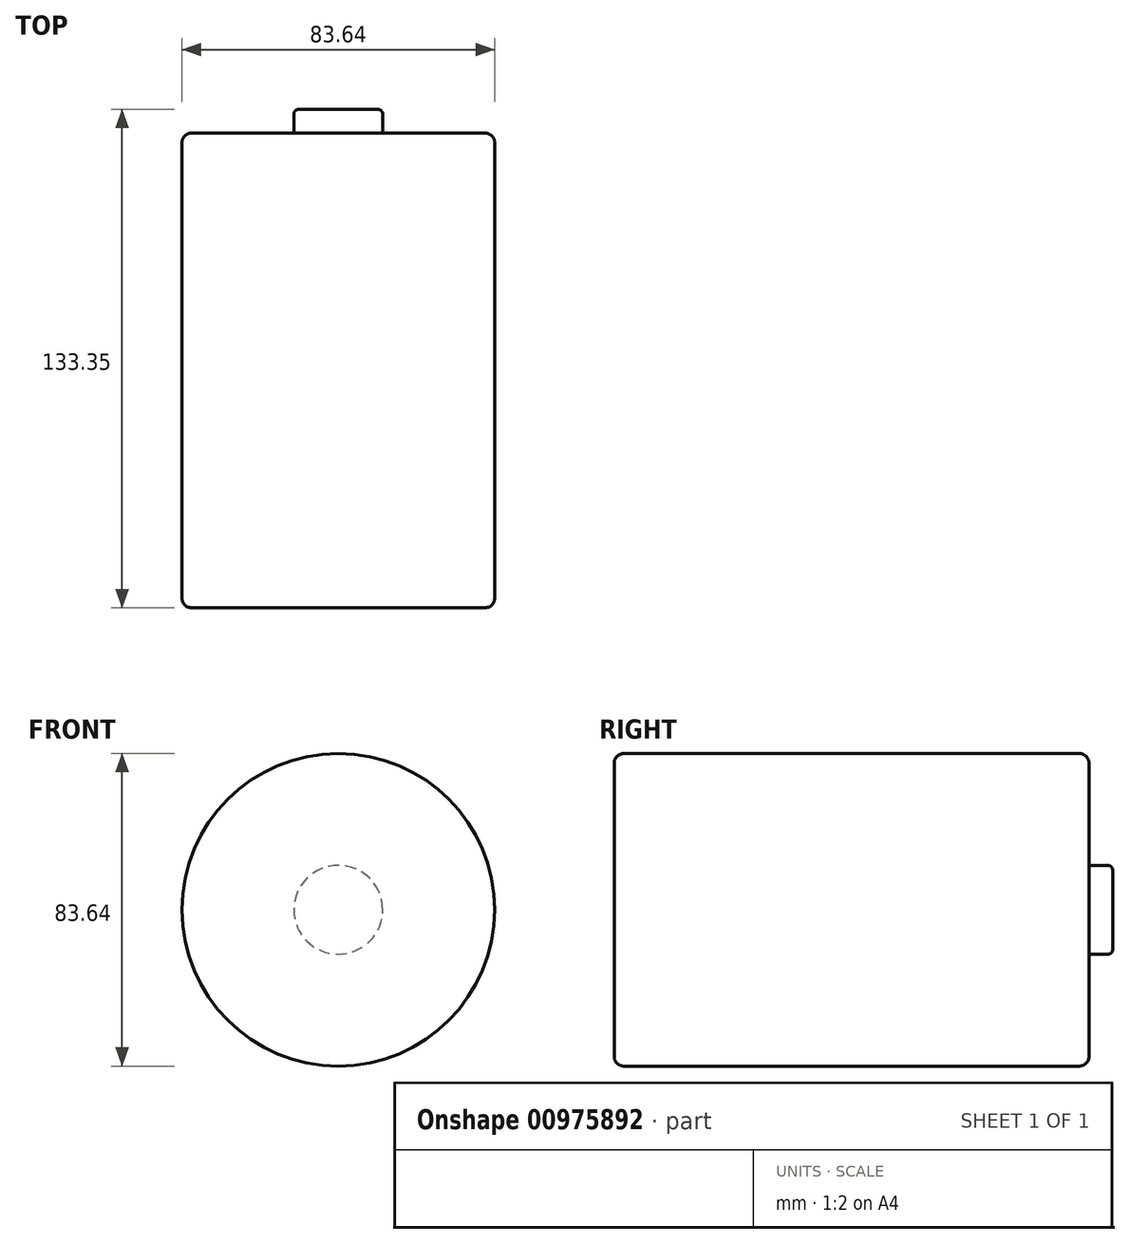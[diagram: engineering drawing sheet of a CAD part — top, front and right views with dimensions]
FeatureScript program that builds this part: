
annotation { "Feature Type Name" : "Feature", "Feature Type Description" : "" }
export const myFeature = defineFeature(function(context is Context, id is Id, definition is map)
    precondition{}
    {
        {
            var Q0;
            Q0=qCreatedBy(makeId("Front.planeOp"),FACE);
            var sketch = newSketch(context, id + "F0", { "sketchPlane" : qUnion([Q0])});
            skCircle(sketch, "E0", {"center": v(0, 0) * mm, "radius": 41.82 * mm});
            skSolve(sketch);
        }
        {
            var Q0;
            Q0=makeQuery(id+"F0.imprint","IMPRINT",FACE,{"disambiguationData":[TD([[makeQuery(id+"F0.imprint","IMPRINT",EDGE,{"derivedFrom":sQuery(id+"F0.wireOp",EDGE,"E0")}),1.0]])]});
            extrude(context, id + "F1", {"entities" : qUnion([Q0]), "depth" : 127 * mm, "offsetDistance" : 25.4 * mm});
        }
        {
            var Q0;
            Q0=makeQuery(id+"F1.opExtrude","CAP_FACE",FACE,{"disambiguationData":[OSD([sQuery(id+"F0.wireOp",EDGE,"E0")])],"isStart":true});
            var sketch = newSketch(context, id + "F2", { "sketchPlane" : qUnion([Q0])});
            skCircle(sketch, "E1", {"center": v(0, 0) * mm, "radius": 11.88 * mm});
            skSolve(sketch);
        }
        {
            var Q0;
            Q0=makeQuery(id+"F2.imprint","IMPRINT",FACE,{"disambiguationData":[TD([[makeQuery(id+"F2.imprint","IMPRINT",EDGE,{"derivedFrom":sQuery(id+"F2.wireOp",EDGE,"E1")}),1.0]])]});
            extrude(context, id + "F3", {"entities" : qUnion([Q0]), "operationType" : NewBodyOperationType.ADD, "depth" : 6.35 * mm, "offsetDistance" : 25.4 * mm});
        }
        {
            var Q0;
            Q0=makeQuery(id+"F1.opExtrude","CAP_EDGE",EDGE,{"disambiguationData":[OSD([sQuery(id+"F0.wireOp",EDGE,"E0")])],"isStart":true});
            fillet(context, id + "F4", {"entities" : qUnion([Q0]), "radius" : 2.54 * mm, "tangentPropagation" : true, "allowEdgeOverflow" : false});
        }
        {
            var Q0;
            Q0=makeQuery(id+"F1.opExtrude","CAP_EDGE",EDGE,{"disambiguationData":[OSD([sQuery(id+"F0.wireOp",EDGE,"E0")])],"isStart":false});
            fillet(context, id + "F5", {"entities" : qUnion([Q0]), "radius" : 2.54 * mm, "tangentPropagation" : true, "allowEdgeOverflow" : false});
        }
        {
            var Q0;
            Q0=makeQuery(id+"F3.opExtrude","CAP_EDGE",EDGE,{"disambiguationData":[OSD([sQuery(id+"F2.wireOp",EDGE,"E1")])],"isStart":false});
            fillet(context, id + "F6", {"entities" : qUnion([Q0]), "radius" : 1.27 * mm, "tangentPropagation" : true, "allowEdgeOverflow" : false});
        }
    });
